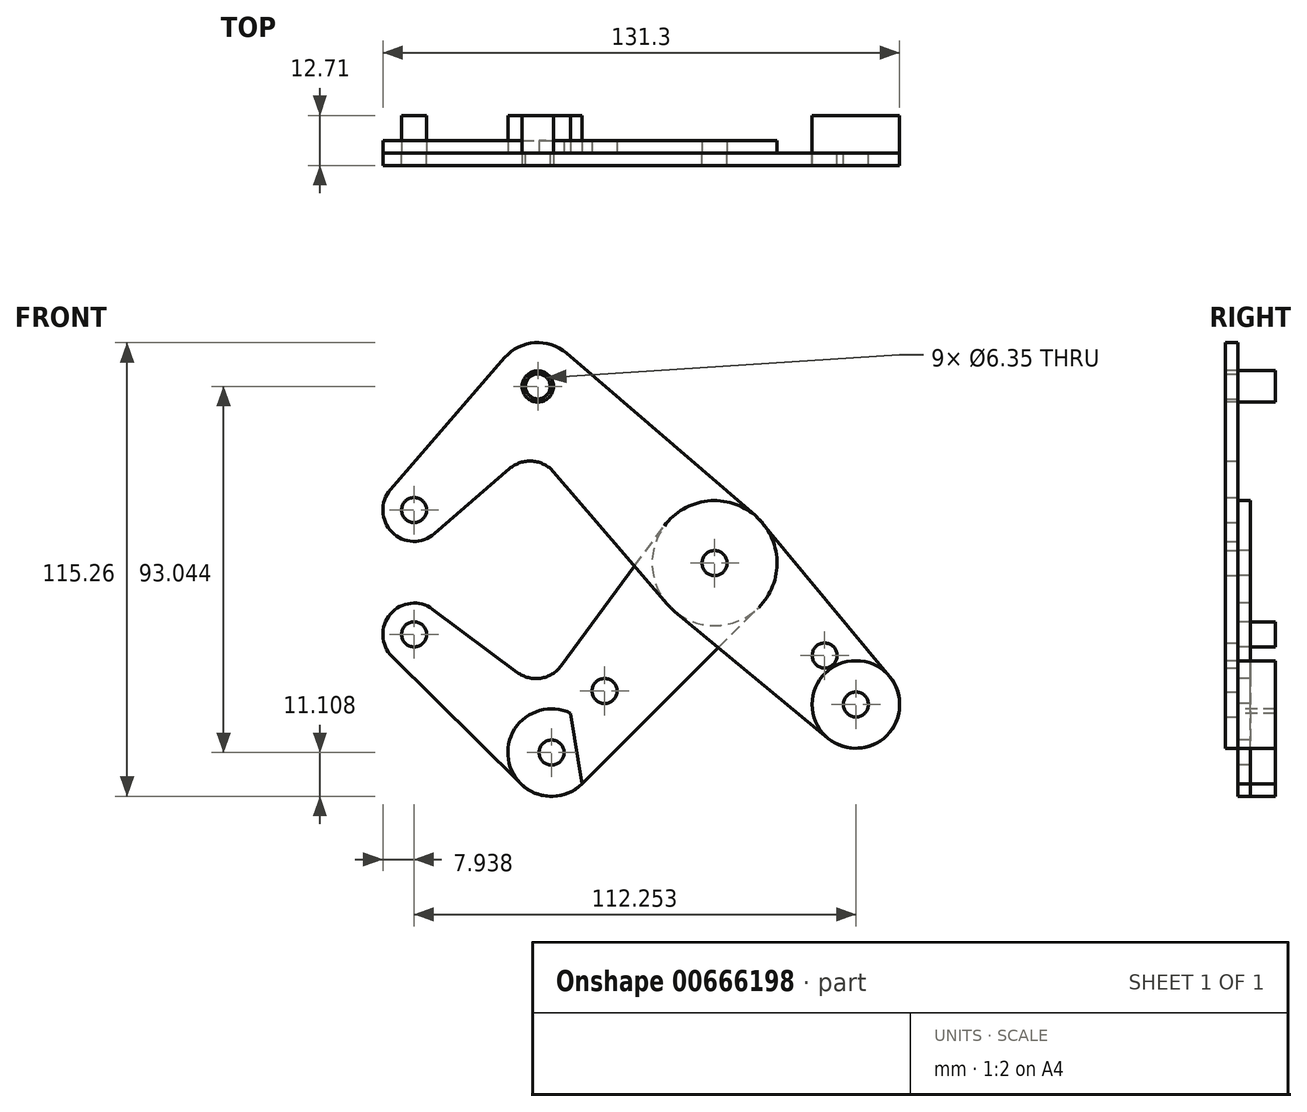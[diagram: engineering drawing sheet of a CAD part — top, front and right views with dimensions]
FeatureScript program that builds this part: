
annotation { "Feature Type Name" : "Feature", "Feature Type Description" : "" }
export const myFeature = defineFeature(function(context is Context, id is Id, definition is map)
    precondition{}
    {
        {
            var Q0;
            Q0=qCreatedBy(makeId("Front.planeOp"),FACE);
            var sketch = newSketch(context, id + "F0", { "sketchPlane" : qUnion([Q0])});
            skLineSegment(sketch, "E0", {"start": v(-76.33, 13.47) * mm, "end": v(-44.9, 44.9) * mm, "construction": true});
            skLineSegment(sketch, "E1", {"start": v(-44.9, 44.9) * mm, "end": v(35.92, -35.92) * mm, "construction": true});
            skCircle(sketch, "E2", {"center": v(-76.33, 13.47) * mm, "radius": 7.94 * mm});
            skCircle(sketch, "E3", {"center": v(-76.33, 13.47) * mm, "radius": 3.18 * mm});
            skCircle(sketch, "E4", {"center": v(-44.9, 44.9) * mm, "radius": 11.11 * mm});
            skCircle(sketch, "E5", {"center": v(-44.9, 44.9) * mm, "radius": 3.18 * mm});
            skCircle(sketch, "E6", {"center": v(0, 0) * mm, "radius": 15.88 * mm});
            skCircle(sketch, "E7", {"center": v(0, 0) * mm, "radius": 3.98 * mm});
            skCircle(sketch, "E8", {"center": v(0, 0) * mm, "radius": 3.18 * mm});
            skCircle(sketch, "E9", {"center": v(35.92, -35.92) * mm, "radius": 11.11 * mm});
            skCircle(sketch, "E10", {"center": v(35.92, -35.92) * mm, "radius": 3.18 * mm});
            skCircle(sketch, "E11", {"center": v(27.97, -23.48) * mm, "radius": 3.18 * mm});
            skLineSegment(sketch, "E12", {"start": v(-82.33, 18.67) * mm, "end": v(-53.3, 52.18) * mm});
            skLineSegment(sketch, "E13", {"start": v(-71.13, 7.47) * mm, "end": v(-52.08, 23.98) * mm});
            skLineSegment(sketch, "E14", {"start": v(-37.66, 53.33) * mm, "end": v(10.35, 12.04) * mm});
            skLineSegment(sketch, "E15", {"start": v(-40.85, 23.15) * mm, "end": v(-12.04, -10.35) * mm});
            skLineSegment(sketch, "E16", {"start": v(28.83, -44.48) * mm, "end": v(-10.12, -12.23) * mm});
            skLineSegment(sketch, "E17", {"start": v(44.48, -28.83) * mm, "end": v(12.23, 10.12) * mm});
            skArc(sketch, "E18.filletArc", {"start": v(-40.85, 23.15) * mm, "mid": v(-46.3, 25.9) * mm, "end": v(-52.08, 23.98) * mm});
            skLineSegment(sketch, "E19", {"start": v(0, 0) * mm, "end": v(-41.4, -48.14) * mm, "construction": true});
            skLineSegment(sketch, "E20", {"start": v(-41.4, -48.14) * mm, "end": v(-76.33, -18.1) * mm, "construction": true});
            skCircle(sketch, "E21", {"center": v(-76.33, -18.1) * mm, "radius": 7.94 * mm});
            skCircle(sketch, "E22", {"center": v(-76.33, -18.1) * mm, "radius": 3.18 * mm});
            skCircle(sketch, "E23", {"center": v(-41.4, -48.14) * mm, "radius": 11.11 * mm});
            skCircle(sketch, "E24", {"center": v(-41.4, -48.14) * mm, "radius": 3.18 * mm});
            skCircle(sketch, "E25", {"center": v(-27.94, -32.49) * mm, "radius": 3.17 * mm});
            skLineSegment(sketch, "E26", {"start": v(-81.91, -23.75) * mm, "end": v(-49.22, -56.05) * mm});
            skLineSegment(sketch, "E27", {"start": v(-71.58, -11.74) * mm, "end": v(-50.13, -27.76) * mm});
            skLineSegment(sketch, "E28", {"start": v(-38.97, -26.11) * mm, "end": v(-12.78, 9.42) * mm});
            skLineSegment(sketch, "E29", {"start": v(-33.55, -56) * mm, "end": v(11.23, -11.23) * mm});
            skPoint(sketch, "E30.newPointA", {"position": v(-33.55, -40.14) * mm});
            skArc(sketch, "E30.filletArc", {"start": v(-50.13, -27.76) * mm, "mid": v(-44.2, -29.26) * mm, "end": v(-38.97, -26.11) * mm});
            skSolve(sketch);
        }
        {
            var Q0;
            {var subQ0=sQuery(id+"F0.wireOp",EDGE,"E12");Q0=makeQuery(id+"F0.imprint","IMPRINT",FACE,{"disambiguationData":[TD([[makeQuery(id+"F0.imprint","IMPRINT",EDGE,{"derivedFrom":subQ0}),-1.0]])]});}
            var Q1;
            Q1=makeQuery(id+"F0.imprint","IMPRINT",FACE,{"disambiguationData":[TD([[makeQuery(id+"F0.imprint","IMPRINT",EDGE,{"derivedFrom":sQuery(id+"F0.wireOp",EDGE,"E3")}),-1.0]])]});
            var Q2;
            Q2=makeQuery(id+"F0.imprint","IMPRINT",FACE,{"disambiguationData":[TD([[makeQuery(id+"F0.imprint","IMPRINT",EDGE,{"derivedFrom":sQuery(id+"F0.wireOp",EDGE,"E5")}),-1.0]])]});
            var Q3;
            {var subQ0=sQuery(id+"F0.wireOp",EDGE,"E16");var subQ1=sQuery(id+"F0.wireOp",EDGE,"E6");var subQ2=makeQuery(id+"F0.imprint","INTERSECT",VERTEX,{"derivedFrom":[subQ1,subQ0]});Q3=makeQuery(id+"F0.imprint","IMPRINT",FACE,{"disambiguationData":[TD([[makeQuery(id+"F0.imprint","IMPRINT",EDGE,{"disambiguationData":[TD([[subQ2,-1.0]])],"derivedFrom":subQ1}),-1.0]])]});}
            var Q4;
            {var subQ0=sQuery(id+"F0.wireOp",EDGE,"E15");var subQ1=sQuery(id+"F0.wireOp",EDGE,"E6");var subQ2=makeQuery(id+"F0.imprint","INTERSECT",VERTEX,{"derivedFrom":[subQ1,subQ0]});Q4=makeQuery(id+"F0.imprint","IMPRINT",FACE,{"disambiguationData":[TD([[makeQuery(id+"F0.imprint","IMPRINT",EDGE,{"disambiguationData":[TD([[subQ2,1.0]])],"derivedFrom":subQ1}),-1.0]])]});}
            var Q5;
            Q5=makeQuery(id+"F0.imprint","IMPRINT",FACE,{"disambiguationData":[TD([[makeQuery(id+"F0.imprint","IMPRINT",EDGE,{"derivedFrom":sQuery(id+"F0.wireOp",EDGE,"E7")}),-1.0]])]});
            var Q6;
            Q6=makeQuery(id+"F0.imprint","IMPRINT",FACE,{"disambiguationData":[TD([[makeQuery(id+"F0.imprint","IMPRINT",EDGE,{"derivedFrom":sQuery(id+"F0.wireOp",EDGE,"E7")}),1.0]])]});
            var Q7;
            Q7=makeQuery(id+"F0.imprint","IMPRINT",FACE,{"disambiguationData":[TD([[makeQuery(id+"F0.imprint","IMPRINT",EDGE,{"derivedFrom":sQuery(id+"F0.wireOp",EDGE,"E11")}),-1.0]])]});
            var Q8;
            Q8=makeQuery(id+"F0.imprint","IMPRINT",FACE,{"disambiguationData":[TD([[makeQuery(id+"F0.imprint","IMPRINT",EDGE,{"derivedFrom":sQuery(id+"F0.wireOp",EDGE,"E10")}),-1.0]])]});
            extrude(context, id + "F1", {"entities" : qUnion([Q0, Q1, Q2, Q3, Q4, Q5, Q6, Q7, Q8]), "depth" : 3.17 * mm, "offsetDistance" : 25.4 * mm});
        }
        {
            var Q0;
            Q0=makeQuery(id+"F0.imprint","IMPRINT",FACE,{"disambiguationData":[TD([[makeQuery(id+"F0.imprint","IMPRINT",EDGE,{"derivedFrom":sQuery(id+"F0.wireOp",EDGE,"E22")}),-1.0]])]});
            var Q1;
            Q1=makeQuery(id+"F0.imprint","IMPRINT",FACE,{"disambiguationData":[TD([[makeQuery(id+"F0.imprint","IMPRINT",EDGE,{"derivedFrom":sQuery(id+"F0.wireOp",EDGE,"E25")}),-1.0]])]});
            var Q2;
            Q2=makeQuery(id+"F0.imprint","IMPRINT",FACE,{"disambiguationData":[TD([[makeQuery(id+"F0.imprint","IMPRINT",EDGE,{"derivedFrom":sQuery(id+"F0.wireOp",EDGE,"E24")}),-1.0]])]});
            var Q3;
            {var subQ0=sQuery(id+"F0.wireOp",EDGE,"E15");var subQ1=sQuery(id+"F0.wireOp",EDGE,"E6");var subQ2=makeQuery(id+"F0.imprint","INTERSECT",VERTEX,{"derivedFrom":[subQ1,subQ0]});Q3=makeQuery(id+"F0.imprint","IMPRINT",FACE,{"disambiguationData":[TD([[makeQuery(id+"F0.imprint","IMPRINT",EDGE,{"disambiguationData":[TD([[subQ2,1.0]])],"derivedFrom":subQ1}),-1.0]])]});}
            var Q4;
            Q4=makeQuery(id+"F0.imprint","IMPRINT",FACE,{"disambiguationData":[TD([[makeQuery(id+"F0.imprint","IMPRINT",EDGE,{"derivedFrom":sQuery(id+"F0.wireOp",EDGE,"E7")}),-1.0]])]});
            var Q5;
            {var subQ0=sQuery(id+"F0.wireOp",EDGE,"E16");var subQ1=sQuery(id+"F0.wireOp",EDGE,"E6");var subQ2=makeQuery(id+"F0.imprint","INTERSECT",VERTEX,{"derivedFrom":[subQ1,subQ0]});Q5=makeQuery(id+"F0.imprint","IMPRINT",FACE,{"disambiguationData":[TD([[makeQuery(id+"F0.imprint","IMPRINT",EDGE,{"disambiguationData":[TD([[subQ2,-1.0]])],"derivedFrom":subQ1}),-1.0]])]});}
            var Q6;
            Q6=makeQuery(id+"F0.imprint","IMPRINT",FACE,{"disambiguationData":[TD([[makeQuery(id+"F0.imprint","IMPRINT",EDGE,{"derivedFrom":sQuery(id+"F0.wireOp",EDGE,"E7")}),1.0]])]});
            extrude(context, id + "F2", {"entities" : qUnion([Q0, Q1, Q2, Q3, Q4, Q5, Q6]), "oppositeDirection" : true, "depth" : 3.17 * mm, "offsetDistance" : 25.4 * mm});
        }
        {
            var Q0;
            Q0=makeQuery(id+"F1.opExtrude","CAP_FACE",FACE,{"disambiguationData":[OSD([sQuery(id+"F0.wireOp",EDGE,"E2"),sQuery(id+"F0.wireOp",EDGE,"E3"),sQuery(id+"F0.wireOp",EDGE,"E4"),sQuery(id+"F0.wireOp",EDGE,"E5"),sQuery(id+"F0.wireOp",EDGE,"E6"),sQuery(id+"F0.wireOp",EDGE,"E8"),sQuery(id+"F0.wireOp",EDGE,"E9"),sQuery(id+"F0.wireOp",EDGE,"E10"),sQuery(id+"F0.wireOp",EDGE,"E11"),sQuery(id+"F0.wireOp",EDGE,"E12"),sQuery(id+"F0.wireOp",EDGE,"E13"),sQuery(id+"F0.wireOp",EDGE,"E14"),sQuery(id+"F0.wireOp",EDGE,"E15"),sQuery(id+"F0.wireOp",EDGE,"E16"),sQuery(id+"F0.wireOp",EDGE,"E17"),sQuery(id+"F0.wireOp",EDGE,"E18.filletArc")])],"isStart":false});
            var sketch = newSketch(context, id + "F3", { "sketchPlane" : qUnion([Q0])});
            skCircle(sketch, "E31", {"center": v(-44.9, 44.9) * mm, "radius": 3.98 * mm});
            skCircle(sketch, "E32", {"center": v(35.92, -35.92) * mm, "radius": 11.11 * mm});
            skSolve(sketch);
        }
        {
            var Q0;
            Q0=makeQuery(id+"F0.imprint","IMPRINT",FACE,{"disambiguationData":[TD([[makeQuery(id+"F0.imprint","IMPRINT",EDGE,{"derivedFrom":sQuery(id+"F0.wireOp",EDGE,"E25")}),-1.0]])]});
            var sketch = newSketch(context, id + "F4", { "sketchPlane" : qUnion([Q0])});
            skCircle(sketch, "E33", {"center": v(-76.33, -18.1) * mm, "radius": 3.18 * mm});
            skArc(sketch, "E34", {"start": v(-36.56, -38.14) * mm, "mid": v(-52.38, -49.88) * mm, "end": v(-33.71, -56.16) * mm});
            skLineSegment(sketch, "E35", {"start": v(-41.4, -48.14) * mm, "end": v(35.92, -35.92) * mm, "construction": true});
            skLineSegment(sketch, "E36", {"start": v(-36.56, -38.14) * mm, "end": v(-33.71, -56.16) * mm});
            skSolve(sketch);
        }
        {
            var Q0;
            Q0=qCreatedBy(makeId("Front.planeOp"),FACE);
            cPlane(context, id + "F5", {"entities" : qUnion([Q0]), "cplaneType" : CPlaneType.OFFSET, "offset" : 9.52 * mm, "oppositeDirection" : true, "width" : 152.4 * mm, "height" : 152.4 * mm});
        }
        {
            var Q0;
            Q0=qSketchRegion(id+"F3",true);
            var Q1;
            Q1=qSketchRegion(id+"F4",true);
            var Q2;
            Q2=qCreatedBy(id+"F5.planeOp",FACE);
            extrude(context, id + "F6", {"entities" : qUnion([Q0, Q1]), "endBound" : BoundingType.UP_TO_SURFACE, "oppositeDirection" : true, "depth" : 25.4 * mm, "endBoundEntityFace" : qUnion([Q2]), "offsetDistance" : 25.4 * mm});
        }
    });
